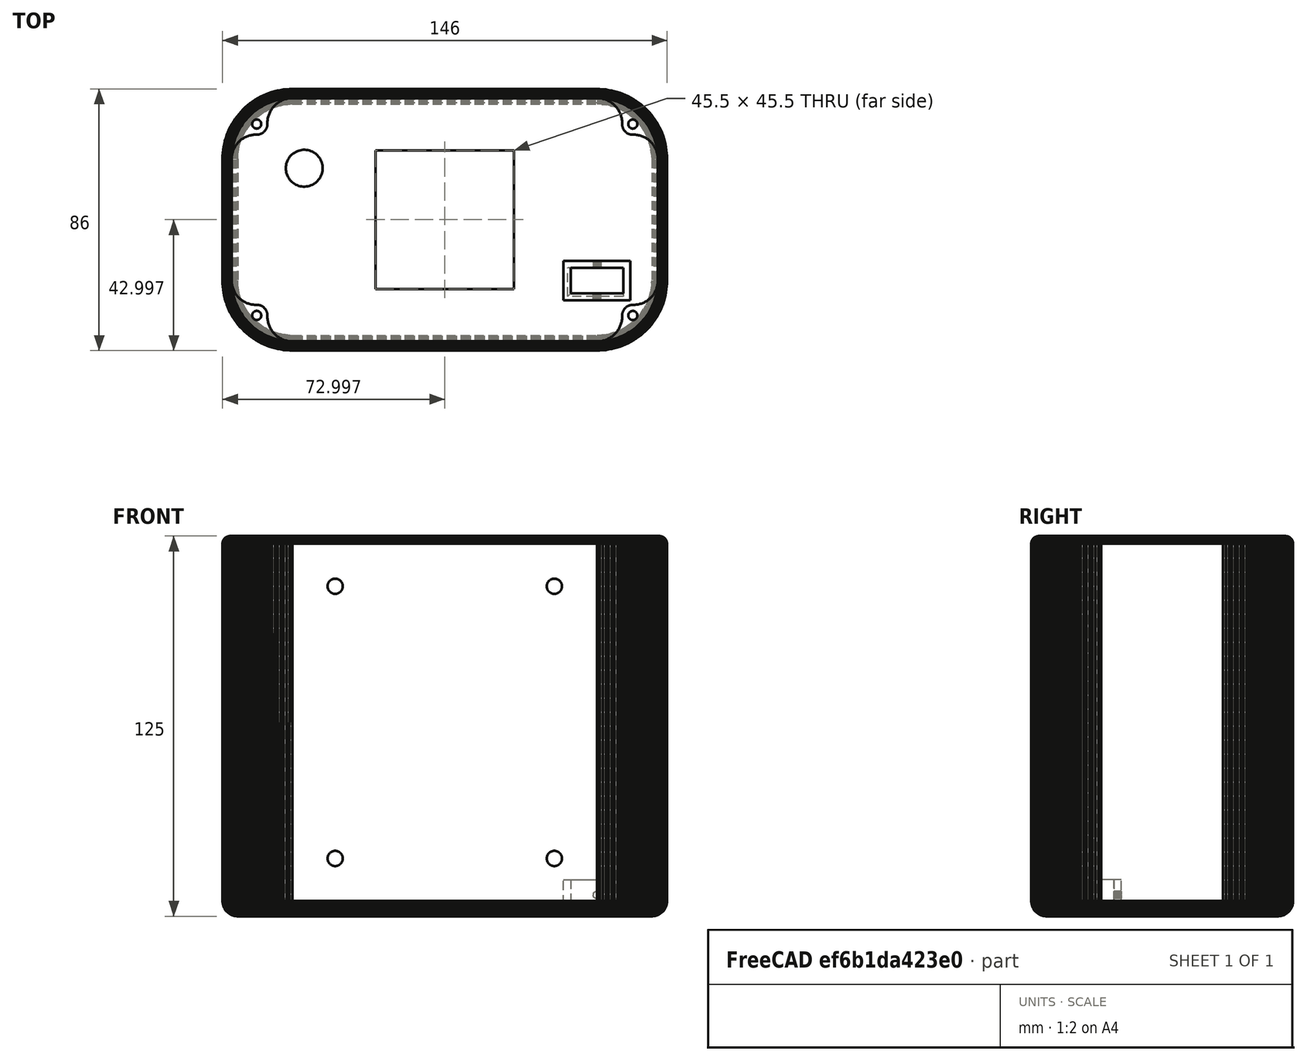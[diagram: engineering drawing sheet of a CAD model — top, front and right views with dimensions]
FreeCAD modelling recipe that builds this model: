
FCSTD DOCUMENT  (FreeCAD 0.18R16093 +53 (Git))
Label: PID Case
License: All rights reserved
LicenseURL: http://en.wikipedia.org/wiki/All_rights_reserved
objects: Sketcher::SketchObject×2, Part::Feature×1, PartDesign::Pad×1, PartDesign::Pocket×1, PartDesign::Chamfer×1, PartDesign::Body×1, Mesh::Feature×1
note: 9 computed .brp shape members not serialized (recipe doc carries the construction recipe); baked Part::Feature solids carry a one-line shape summary decoded from their .brp

FEATURE [Part::Feature] PIDFrontCase_Fixed001_solid001  label="PIDFrontCase_Fixed001 (Solid)001"
  shape: large baked B-rep (33 MB .brp); summary skipped
FEATURE [Sketcher::SketchObject] Sketch
  MapMode = 5
  Placement = pos=(0,0,-8.9407e-07) rot=(1,0,0;3.14159rad)
  Support = -> [PIDFrontCase_Fixed001_solid001]
  sketch-geometry (4):
    g0: LineSegment StartX=-53.7959 StartY=-8.35645 StartZ=0 EndX=-36 EndY=-8.35645 EndZ=0
    g1: LineSegment StartX=-36 StartY=-8.35645 StartZ=0 EndX=-36 EndY=-32.4084 EndZ=0
    g2: LineSegment StartX=-36 StartY=-32.4084 StartZ=0 EndX=-53.7959 EndY=-32.4084 EndZ=0
    g3: LineSegment StartX=-53.7959 StartY=-32.4084 StartZ=0 EndX=-53.7959 EndY=-8.35645 EndZ=0
  constraints (8):
    c: Coincident(g0,g1)
    c: Coincident(g1,g2)
    c: Coincident(g2,g3)
    c: Coincident(g3,g0)
    c: Horizontal(g0)
    c: Horizontal(g2)
    c: Vertical(g1)
    c: Vertical(g3)
FEATURE [PartDesign::Pad] Pad
  Length = 10
  Length2 = 100
  Profile = -> Sketch
  Reversed = true
  Type = 3
  UpToFace = -> PIDFrontCase_Fixed001_solid001 [Face21373]
FEATURE [Sketcher::SketchObject] Sketch001
  MapMode = 5
  Placement = pos=(0,0,-8.9407e-07) rot=(1,0,0;3.14159rad)
  Support = -> [Pad]
  sketch-geometry (1):
    g0: Circle CenterX=-40.7823 CenterY=-17.0112 CenterZ=0 NormalX=0 NormalY=0 NormalZ=1 AngleXU=0 Radius=6.05
  constraints (1):
    c: Radius(g0) = 6.05
FEATURE [PartDesign::Pocket] Pocket
  BaseFeature = -> Pad
  Length = 5
  Length2 = 100
  Profile = -> Sketch001
  Type = 1
FEATURE [PartDesign::Chamfer] Chamfer
  Base = -> Pocket [Edge2230,Edge2229,Edge2231,Edge2232]
  BaseFeature = -> Pocket
  Size = 1
FEATURE [PartDesign::Body] Body
  Group = -> [PIDFrontCase_Fixed001_solid001,Sketch,Pad,Sketch001,Pocket,Chamfer]
  Origin = -> Origin
  Tip = -> Chamfer
FEATURE [Mesh::Feature] Mesh  label="Chamfer (Meshed)"
